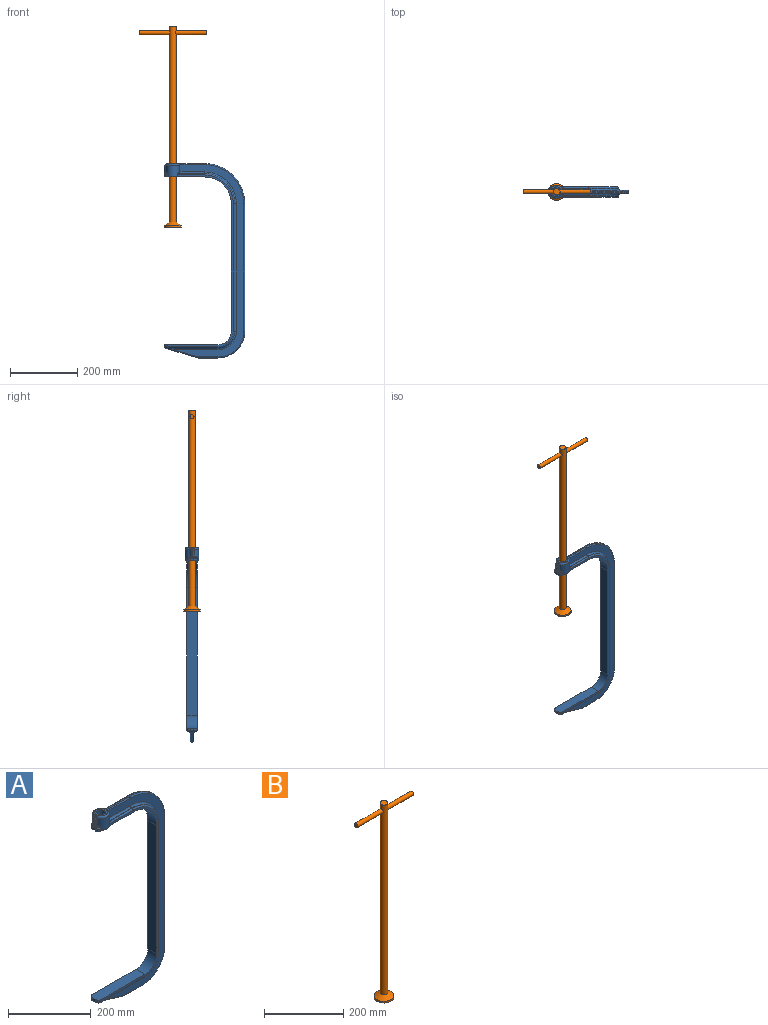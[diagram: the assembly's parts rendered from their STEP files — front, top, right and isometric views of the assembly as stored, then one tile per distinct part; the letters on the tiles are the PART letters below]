
ASSEMBLY  parts=2 mates=1
PART A: 139 faces, bbox 251.7x44.3x597.5 mm
  f0: plane 512x196mm, normal (0,1,0), area 4851.6mm2, adj f4,f20,f21,f22,f23,f24,f30,f41
  f1: plane 512x196mm, normal (0,-1,0), area 4851.6mm2, adj f20,f21,f22,f23,f24,f31,f33,f34
  f2: plane 74.8x1mm, normal (0,0,1), area 74.5mm2, adj f9,f25,f40,f120
  f3: cylinder r=4mm len=1.57mm, axis (1,0,0), area 0.6mm2, adj f18,f42,f114
  f4: cylinder r=4mm len=80.68mm, axis (-1,0,0), area 488.5mm2, adj f0,f10,f47,f128
  f5: plane 17.82x0.44mm, normal (0,-1,0), area 7.4mm2, adj f70,f71,f82,f111
  f6: plane 17.82x0.44mm, normal (0,1,0), area 7.4mm2, adj f78,f79,f101,f133
  f7: cylinder r=3mm len=0.13mm, axis (1,0,0), area 0mm2, adj f55,f70,f108
  f8: cylinder r=3mm len=80.13mm, axis (-1,0,0), area 362.5mm2, adj f54,f55,f76,f123
  f9: cylinder r=5mm len=74.29mm, axis (1,0,0), area 580.1mm2, adj f2,f53,f83,f119
  f10: plane 74.8x1mm, normal (0,0,1), area 74.5mm2, adj f4,f11,f100,f127
  f11: cylinder r=90mm len=90mm, axis (0,-1,0), area 141.4mm2, adj f10,f12,f47,f99
  f12: plane 380x1mm, normal (1,0,0), area 380mm2, adj f11,f13,f45,f98
  f13: cylinder r=50mm len=50mm, axis (0,-1,0), area 78.5mm2, adj f12,f28,f43,f97
  f14: plane 156.58x5.43mm, normal (0,0,-1), area 172.8mm2, adj f27,f33,f35,f86,f87,f88
  f15: cylinder r=4mm len=3mm, axis (0,-1,0), area 2.2mm2, adj f19,f42,f80
  f16: plane 6x0.68mm, normal (0,1,0), area 4.1mm2, adj f20,f29,f48,f137
  f17: plane 10x6mm, normal (-1,0,0), area 60mm2, adj f24,f30,f31,f37
  f18: plane 6x0.68mm, normal (0,-1,0), area 4.1mm2, adj f3,f20,f32,f115
  f19: plane 30x10mm, normal (-1,0,0), area 156mm2, adj f15,f20,f29,f32,f44,f63,f71,f79
  f20: plane 120x40mm, normal (0,0,-1), area 3424.8mm2, adj f0,f1,f16,f18,f19,f21,f29,f32
  f21: cylinder r=80mm len=80mm, axis (0,-1,0), area 3769.9mm2, adj f0,f1,f20,f22
  f22: plane 380x30mm, normal (-1,0,0), area 11400mm2, adj f0,f1,f21,f23
  f23: cylinder r=40mm len=40mm, axis (0,-1,0), area 1885mm2, adj f0,f1,f22,f24
  f24: plane 160x30mm, normal (0,0,1), area 4757.1mm2, adj f0,f1,f17,f23,f30,f31
  f25: cylinder r=90mm len=90mm, axis (0,-1,0), area 141.4mm2, adj f2,f26,f38,f83
  f26: plane 380x1mm, normal (1,0,0), area 380mm2, adj f25,f27,f36,f84
  f27: cylinder r=50mm len=50mm, axis (0,-1,0), area 78.5mm2, adj f14,f26,f34,f85
  f28: plane 156.87x5.72mm, normal (0,0,-1), area 172.8mm2, adj f13,f39,f41,f94,f95,f96
  f29: cylinder r=10mm len=10mm, axis (0,0,1), area 94.2mm2, adj f16,f19,f20,f46
  f30: cylinder r=10mm len=10mm, axis (0,0,1), area 94.2mm2, adj f0,f17,f24,f39
  f31: cylinder r=10mm len=10mm, axis (0,0,-1), area 94.2mm2, adj f1,f17,f24,f35
  f32: cylinder r=10mm len=10mm, axis (0,0,-1), area 94.2mm2, adj f18,f19,f20,f42
  f33: cylinder r=4mm len=150mm, axis (-1,0,0), area 942.5mm2, adj f1,f14,f34,f35
  f34: torus R=46mm, axis (0,1,0), area 479.1mm2, adj f1,f27,f33,f36
  f35: torus R=6mm, axis (0,0,1), area 83.9mm2, adj f14,f31,f33,f37,f89
  f36: cylinder r=4mm len=380mm, axis (0,0,-1), area 2387.6mm2, adj f1,f26,f34,f38
  f37: cylinder r=4mm len=10mm, axis (0,1,0), area 50.7mm2, adj f17,f35,f39,f90,f91,f92
  f38: torus R=86mm, axis (0,1,0), area 873.9mm2, adj f1,f25,f36,f40
  f39: torus R=6mm, axis (0,0,1), area 83.9mm2, adj f28,f30,f37,f41,f93
  f40: cylinder r=4mm len=80.68mm, axis (1,0,0), area 488.5mm2, adj f1,f2,f38,f121
  f41: cylinder r=4mm len=150mm, axis (1,0,0), area 942.5mm2, adj f0,f28,f39,f43
  f42: torus R=6mm, axis (0,0,-1), area 56.6mm2, adj f3,f15,f32,f81,f82,f113
  f43: torus R=46mm, axis (0,1,0), area 479.1mm2, adj f0,f13,f41,f45
  f44: cylinder r=4mm len=3mm, axis (0,-1,0), area 2.2mm2, adj f19,f46,f103
  f45: cylinder r=4mm len=380mm, axis (0,0,1), area 2387.6mm2, adj f0,f12,f43,f47
  f46: torus R=6mm, axis (0,0,-1), area 56.6mm2, adj f29,f44,f48,f101,f102,f135
  f47: torus R=86mm, axis (0,1,0), area 873.9mm2, adj f0,f4,f11,f45
  f48: cylinder r=4mm len=1.57mm, axis (-1,0,0), area 0.6mm2, adj f16,f46,f136
  f49: cylinder r=3mm len=92.33mm, axis (-0.96,0,0.29), area 424.7mm2, adj f51,f53,f60,f64,f87
  f50: cylinder r=3mm len=92.33mm, axis (-0.96,0,0.29), area 424.7mm2, adj f52,f54,f60,f72,f95
  f51: torus R=7mm, axis (0,1,0), area 5mm2, adj f49,f62,f88,f89,f90
  f52: torus R=7mm, axis (0,1,0), area 5mm2, adj f50,f62,f92,f93,f94
  f53: plane 574x209.89mm, normal (0,-1,0), area 18036.6mm2, adj f9,f49,f64,f65,f66,f67,f68,f69
  f54: plane 574x209.89mm, normal (0,1,0), area 18036.6mm2, adj f8,f50,f72,f73,f74,f75,f76,f96
  f55: plane 110x30mm, normal (0,0,1), area 713.1mm2, adj f7,f8,f56,f63,f69,f77,f105,f106
  f56: cylinder r=120mm len=120mm, axis (0,-1,0), area 754mm2, adj f55,f57,f68,f76
  f57: plane 380x4mm, normal (1,0,0), area 1520mm2, adj f56,f58,f67,f75
  f58: cylinder r=80mm len=80mm, axis (0,-1,0), area 502.7mm2, adj f57,f59,f66,f74
  f59: plane 58.53x4mm, normal (0,0,-1), area 234.1mm2, adj f58,f61,f65,f73
  f60: plane 91.47x27.44mm, normal (-0.29,0,-0.96), area 382mm2, adj f49,f50,f61,f62
  f61: cylinder r=10mm len=4mm, axis (0,-1,0), area 11.7mm2, adj f59,f60,f64,f72
  f62: cylinder r=10mm len=4mm, axis (0,-1,0), area 14.7mm2, adj f51,f52,f60,f91
  f63: cylinder r=10mm len=10mm, axis (0,-1,0), area 62.8mm2, adj f19,f55,f70,f78
  f64: torus R=7mm, axis (0,1,0), area 12.2mm2, adj f49,f53,f61,f65
  f65: cylinder r=3mm len=58.53mm, axis (-1,0,0), area 275.8mm2, adj f53,f59,f64,f66
  f66: torus R=77mm, axis (0,1,0), area 584.1mm2, adj f53,f58,f65,f67
  f67: cylinder r=3mm len=380mm, axis (0,0,-1), area 1790.7mm2, adj f53,f57,f66,f68
  f68: torus R=117mm, axis (0,1,0), area 880.2mm2, adj f53,f56,f67,f69
  f69: cylinder r=3mm len=80.13mm, axis (1,0,0), area 362.5mm2, adj f53,f55,f68,f116
  f70: torus R=7mm, axis (0,1,0), area 45.4mm2, adj f5,f7,f63,f71,f109,f110
  f71: cylinder r=3mm len=24mm, axis (0,0,-1), area 90.3mm2, adj f5,f19,f70,f80,f81
  f72: torus R=7mm, axis (0,1,0), area 12.2mm2, adj f50,f54,f61,f73
  f73: cylinder r=3mm len=58.53mm, axis (1,0,0), area 275.8mm2, adj f54,f59,f72,f74
  f74: torus R=77mm, axis (0,1,0), area 584.1mm2, adj f54,f58,f73,f75
  f75: cylinder r=3mm len=380mm, axis (0,0,1), area 1790.7mm2, adj f54,f57,f74,f76
  f76: torus R=117mm, axis (0,1,0), area 880.2mm2, adj f8,f54,f56,f75
  f77: cylinder r=3mm len=0.13mm, axis (-1,0,0), area 0mm2, adj f55,f78,f130
  f78: torus R=7mm, axis (0,1,0), area 45.4mm2, adj f6,f63,f77,f79,f131,f132
  f79: cylinder r=3mm len=24mm, axis (0,0,1), area 90.3mm2, adj f6,f19,f78,f102,f103
  f80: bspline ~4.18x3.93mm, area 2.7mm2, adj f15,f71,f81
  f81: bspline ~7.6x6.33mm, area 26.5mm2, adj f42,f71,f80,f82
  f82: bspline ~5.19x4.54mm, area 2.3mm2, adj f5,f42,f81,f112
  f83: torus R=95mm, axis (0,1,0), area 1132.7mm2, adj f9,f25,f53,f84
  f84: cylinder r=5mm len=380mm, axis (0,0,-1), area 2984.5mm2, adj f26,f53,f83,f85
  f85: torus R=55mm, axis (0,1,0), area 639.3mm2, adj f27,f53,f84,f86
  f86: cylinder r=5mm len=132.89mm, axis (-1,0,0), area 1043.7mm2, adj f14,f53,f85,f87
  f87: bspline ~20.84x6.01mm, area 121.1mm2, adj f14,f49,f86,f88
  f88: bspline ~5.06x4.32mm, area 6.9mm2, adj f14,f51,f87,f89
  f89: bspline ~4.07x3.39mm, area 3.9mm2, adj f35,f51,f88,f90
  f90: bspline ~4.54x2.98mm, area 4.5mm2, adj f37,f51,f89,f91
  f91: cylinder r=5mm len=4mm, axis (0,-1,0), area 5.9mm2, adj f37,f62,f90,f92
  f92: bspline ~4.54x2.98mm, area 4.5mm2, adj f37,f52,f91,f93
  f93: bspline ~5.15x4.38mm, area 3.9mm2, adj f39,f52,f92,f94
  f94: bspline ~5.06x4.32mm, area 6.9mm2, adj f28,f52,f93,f95
  f95: bspline ~20.84x6.01mm, area 121.1mm2, adj f28,f50,f94,f96
  f96: cylinder r=5mm len=132.89mm, axis (-1,0,0), area 1043.7mm2, adj f28,f54,f95,f97
  f97: torus R=55mm, axis (0,1,0), area 639.3mm2, adj f13,f54,f96,f98
  f98: cylinder r=5mm len=380mm, axis (0,0,-1), area 2984.5mm2, adj f12,f54,f97,f99
  f99: torus R=95mm, axis (0,1,0), area 1132.7mm2, adj f11,f54,f98,f100
  f100: cylinder r=5mm len=74.29mm, axis (1,0,0), area 580.1mm2, adj f10,f54,f99,f126
  f101: bspline ~5.19x4.54mm, area 2.3mm2, adj f6,f46,f102,f134
  f102: bspline ~7.6x6.33mm, area 26.5mm2, adj f46,f79,f101,f103
  f103: bspline ~4.18x3.93mm, area 2.7mm2, adj f44,f79,f102
  f104: cylinder r=20mm len=37.55mm, axis (0,0,-1), area 1446.8mm2, adj f20,f105,f125,f126,f127,f128,f129,f132
  f105: torus R=15mm, axis (0,0,-1), area 365.6mm2, adj f55,f104,f123,f124,f130,f131
  f106: torus R=15mm, axis (0,0,-1), area 365.6mm2, adj f55,f107,f108,f109,f116,f117
  f107: cylinder r=20mm len=37.55mm, axis (0,0,-1), area 1446.8mm2, adj f20,f106,f110,f111,f112,f113,f114,f115
  f108: bspline ~0.4x0.37mm, area 0mm2, adj f7,f106,f109
  f109: bspline ~6.33x6.24mm, area 14.2mm2, adj f70,f106,f108,f110
  f110: bspline ~5.41x2.97mm, area 8mm2, adj f70,f107,f109,f111
  f111: cylinder r=3mm len=17.72mm, axis (0,0,-1), area 64.6mm2, adj f5,f107,f110,f112
  f112: bspline ~5.92x5.16mm, area 18.7mm2, adj f82,f107,f111,f113
  f113: bspline ~8.14x8mm, area 28.9mm2, adj f42,f107,f112,f114
  f114: bspline ~4.73x2.99mm, area 5mm2, adj f3,f107,f113,f115
  f115: cylinder r=3mm len=6mm, axis (0,0,-1), area 12.1mm2, adj f18,f20,f107,f114
  f116: bspline ~6.71x4.99mm, area 9.3mm2, adj f69,f106,f117
  f117: bspline ~5.32x3.41mm, area 5.8mm2, adj f53,f106,f116,f118
  f118: cylinder r=3mm len=20mm, axis (0,0,-1), area 72.9mm2, adj f53,f107,f117,f119
  f119: bspline ~6.27x6.24mm, area 23.3mm2, adj f9,f107,f118,f120
  f120: torus R=23mm, axis (0,0,-1), area 4.9mm2, adj f2,f107,f119,f121
  f121: bspline ~8.2x7.96mm, area 31.6mm2, adj f40,f107,f120,f122
  f122: cylinder r=3mm len=6mm, axis (0,0,-1), area 12.1mm2, adj f1,f20,f107,f121
  f123: bspline ~6.71x4.99mm, area 9.3mm2, adj f8,f105,f124
  f124: bspline ~5.32x3.41mm, area 5.8mm2, adj f54,f105,f123,f125
  f125: cylinder r=3mm len=20mm, axis (0,0,-1), area 72.9mm2, adj f54,f104,f124,f126
  f126: bspline ~6.27x6.24mm, area 23.3mm2, adj f100,f104,f125,f127
  f127: torus R=23mm, axis (0,0,-1), area 4.9mm2, adj f10,f104,f126,f128
  f128: bspline ~8.51x8.2mm, area 31.6mm2, adj f4,f104,f127,f129
  f129: cylinder r=3mm len=6mm, axis (0,0,-1), area 12.1mm2, adj f0,f20,f104,f128
  f130: bspline ~0.4x0.37mm, area 0mm2, adj f77,f105,f131
  f131: bspline ~6.77x6.38mm, area 14.2mm2, adj f78,f105,f130,f132
  f132: bspline ~5.41x2.97mm, area 8mm2, adj f78,f104,f131,f133
  f133: cylinder r=3mm len=17.72mm, axis (0,0,-1), area 64.6mm2, adj f6,f104,f132,f134
  f134: bspline ~5.95x5.13mm, area 18.7mm2, adj f101,f104,f133,f135
  f135: bspline ~8.14x8mm, area 28.9mm2, adj f46,f104,f134,f136
  f136: bspline ~3.83x2.99mm, area 5mm2, adj f48,f104,f135,f137
  f137: cylinder r=3mm len=6mm, axis (0,0,-1), area 12.1mm2, adj f16,f20,f104,f136
  f138: cylinder r=10mm len=40mm, axis (0,0,1), area 2513.3mm2, adj f20,f55
PART B: 9 faces, bbox 200x50x600 mm
  f0: cylinder r=25mm len=50mm, axis (0,0,1), area 785.4mm2, adj f1,f4
  f1: cone r=25mm half-angle=56.3deg, axis (0,0,-1), area 1982.3mm2, adj f0,f2
  f2: cylinder r=10mm len=585mm, axis (0,0,1), area 36518.8mm2, adj f1,f3,f6,f7
  f3: plane 20x20mm, normal (0,0,1), area 314.2mm2, adj f2
  f4: plane 50x50mm, normal (0,0,-1), area 1963.5mm2, adj f0
  f5: plane 12x12mm, normal (-1,0,0), area 113.1mm2, adj f6
  f6: cylinder r=6mm len=92mm, axis (-1,0,0), area 3429.6mm2, adj f2,f5
  f7: cylinder r=6mm len=92mm, axis (-1,0,0), area 3429.6mm2, adj f2,f8
  f8: plane 12x12mm, normal (1,0,0), area 113.1mm2, adj f7
PLACE A t=(2393.19,-326.94,-442.37)mm
PLACE B t=(2906.22,-326.94,-426.59)mm
MATE cylindrical B.f0 <-> A.f104  axis (0,0,1) through (1171.04,-326.94,707.28)mm
